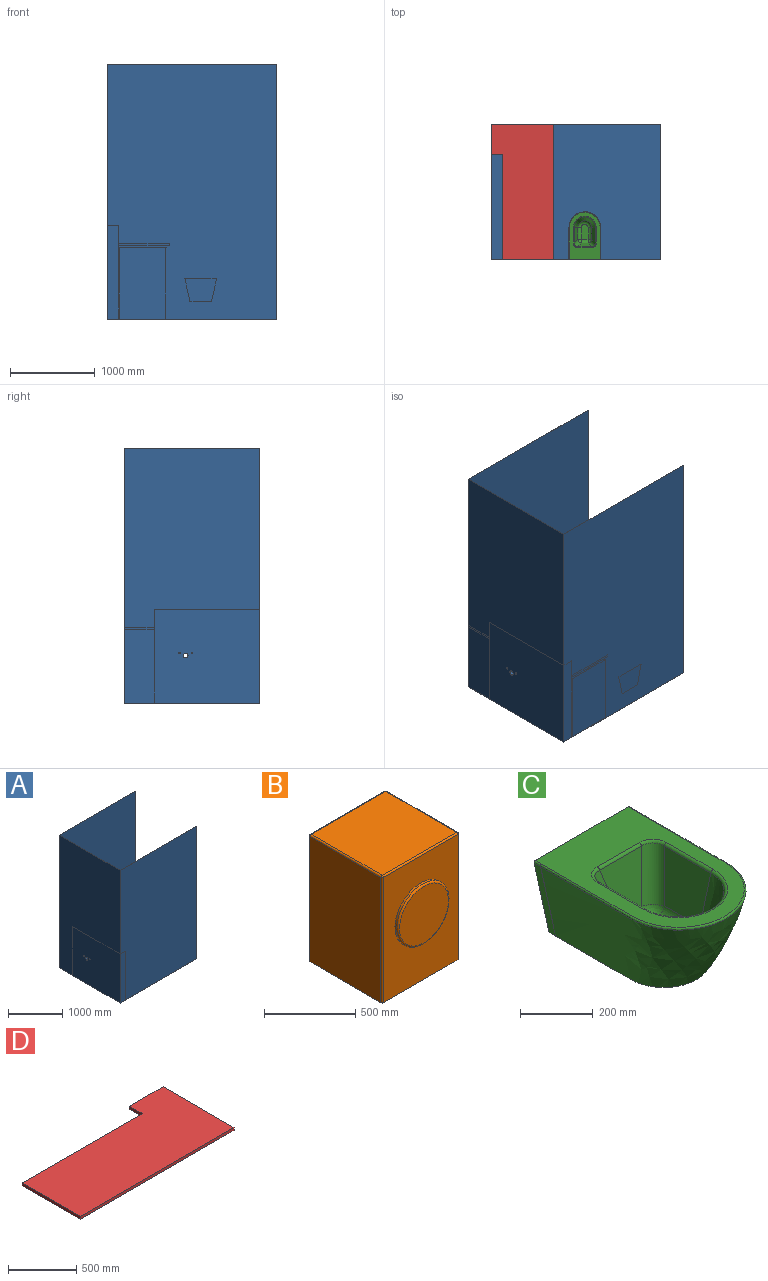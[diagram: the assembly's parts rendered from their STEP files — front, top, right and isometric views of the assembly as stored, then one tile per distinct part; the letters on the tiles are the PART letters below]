
ASSEMBLY  parts=4 mates=3
PART A: 30 faces, bbox 2000x1593x3000 mm
  f0: plane 27x12.73mm, normal (1,0,0), area 104.7mm2, adj f15,f18,f19
  f1: plane 645x85mm, normal (1,0,0), area 51115.5mm2, adj f10,f15,f17,f18,f19
  f2: plane 1999x1591mm, normal (0,0,1), area 3016465mm2, adj f3,f5,f10,f11,f12,f13
  f3: plane 2999x1591mm, normal (1,0,0), area 3398999mm2, adj f2,f4,f10,f11,f13,f14
  f4: plane 2000x1593mm, normal (0,0,1), area 5591mm2, adj f3,f5,f6,f7,f8,f10,f11
  f5: plane 3000x1593mm, normal (1,0,0), area 7591mm2, adj f2,f4,f6,f8,f9,f10,f11
  f6: plane 3000x2000mm, normal (0,1,0), area 6000000mm2, adj f4,f5,f7,f9
  f7: plane 3000x1593mm, normal (-1,0,0), area 4776115.2mm2, adj f4,f6,f8,f9,f22,f28,f29
  f8: plane 3000x2000mm, normal (0,-1,0), area 6000000mm2, adj f4,f5,f7,f9
  f9: plane 2000x1593mm, normal (0,0,-1), area 3186000mm2, adj f5,f6,f7,f8
  f10: plane 2999x1999mm, normal (0,-1,0), area 5733776mm2, adj f1,f2,f3,f4,f5,f15,f16,f17
  f11: plane 2999x1999mm, normal (0,1,0), area 5849141mm2, adj f2,f3,f4,f5,f12,f14
  f12: plane 1242x1105mm, normal (1,0,0), area 1369525.2mm2, adj f2,f11,f13,f14,f22,f28,f29
  f13: plane 1105x132mm, normal (0,1,0), area 145860mm2, adj f2,f3,f12,f14
  f14: plane 1242x132mm, normal (0,0,1), area 163944mm2, adj f3,f11,f12,f13
  f15: plane 405x85mm, normal (0,0,1), area 34425mm2, adj f0,f1,f10,f16,f18,f21
  f16: plane 645x85mm, normal (-1,0,0), area 54825mm2, adj f10,f15,f17,f18
  f17: plane 405x85mm, normal (0,0,-1), area 34425mm2, adj f1,f10,f16,f18
  f18: plane 645x405mm, normal (0,-1,0), area 256950mm2, adj f0,f1,f15,f16,f17,f23,f24,f25
  f19: cylinder r=35mm len=95mm, axis (-1,0,0), area 20891.6mm2, adj f0,f1,f20,f21
  f20: plane 70x70mm, normal (1,0,0), area 3848.5mm2, adj f19
  f21: plane 44.54x8mm, normal (-1,0,0), area 243.6mm2, adj f15,f19
  f22: cylinder r=27.5mm len=133mm, axis (1,0,0), area 22980.8mm2, adj f7,f12
  f23: plane 45x30mm, normal (0,0,1), area 1350mm2, adj f18,f24,f26,f27
  f24: plane 95x30mm, normal (-1,0,0), area 2850mm2, adj f18,f23,f25,f27
  f25: plane 45x30mm, normal (0,0,-1), area 1350mm2, adj f18,f24,f26,f27
  f26: plane 95x30mm, normal (1,0,0), area 2850mm2, adj f18,f23,f25,f27
  f27: plane 95x45mm, normal (0,-1,0), area 4275mm2, adj f23,f24,f25,f26
  f28: cylinder r=9mm len=133mm, axis (1,0,0), area 7521mm2, adj f7,f12
  f29: cylinder r=9mm len=133mm, axis (1,0,0), area 7521mm2, adj f7,f12
PART B: 21 faces, bbox 597x595x850 mm
  f0: plane 577x550mm, normal (0,0,1), area 317350mm2, adj f11,f14,f17,f20
  f1: plane 840x550mm, normal (-1,0,0), area 462000mm2, adj f2,f15,f16,f20
  f2: plane 597x570mm, normal (0,0,-1), area 340204.2mm2, adj f1,f3,f4,f5,f9,f10,f15,f16
  f3: plane 840x550mm, normal (1,0,0), area 462000mm2, adj f2,f9,f10,f11
  f4: plane 840x577mm, normal (0,-1,0), area 359016.3mm2, adj f2,f6,f9,f14,f15
  f5: plane 840x577mm, normal (0,1,0), area 484680mm2, adj f2,f10,f16,f17
  f6: cylinder r=200mm len=400mm, axis (0,1,0), area 18221.2mm2, adj f4,f8
  f7: plane 379x379mm, normal (0,-1,0), area 112815.4mm2, adj f8
  f8: torus R=189.5mm, axis (0,-1,0), area 20330.8mm2, adj f6,f7
  f9: cylinder r=10mm len=840mm, axis (0,0,-1), area 13194.7mm2, adj f2,f3,f4,f12
  f10: cylinder r=10mm len=840mm, axis (0,0,1), area 13194.7mm2, adj f2,f3,f5,f13
  f11: cylinder r=10mm len=550mm, axis (0,1,0), area 8639.4mm2, adj f0,f3,f12,f13
  f12: sphere r=10mm, area 157.1mm2, adj f9,f11,f14
  f13: sphere r=10mm, area 157.1mm2, adj f10,f11,f17
  f14: cylinder r=10mm len=577mm, axis (1,0,0), area 9063.5mm2, adj f0,f4,f12,f18
  f15: cylinder r=10mm len=840mm, axis (0,0,1), area 13194.7mm2, adj f1,f2,f4,f18
  f16: cylinder r=10mm len=840mm, axis (0,0,-1), area 13194.7mm2, adj f1,f2,f5,f19
  f17: cylinder r=10mm len=577mm, axis (-1,0,0), area 9063.5mm2, adj f0,f5,f13,f19
  f18: sphere r=10mm, area 157.1mm2, adj f14,f15,f20
  f19: sphere r=10mm, area 157.1mm2, adj f16,f17,f20
  f20: cylinder r=10mm len=550mm, axis (0,-1,0), area 8639.4mm2, adj f0,f1,f18,f19
PART C: 30 faces, bbox 409.3x644.8x304.3 mm
  f0: plane 558.49x362.53mm, normal (0,0,1), area 97226.2mm2, adj f3,f6,f7,f8,f9,f10,f24,f25
  f1: plane 453.07x260.57mm, normal (0,0,-1), area 107135mm2, adj f2,f4,f5,f7
  f2: bspline ~565x375mm, area 311654.4mm2, adj f1,f3,f6,f8
  f3: plane 304.29x93.05mm, normal (0,-1,0), area 190.7mm2, adj f0,f2,f4,f8,f10
  f4: plane 263.92x58.65mm, normal (0.98,0,-0.22), area 6758.8mm2, adj f1,f3,f7,f10
  f5: plane 263.92x58.65mm, normal (-0.98,0,-0.22), area 6758.8mm2, adj f1,f6,f7,f9
  f6: plane 304.29x93.05mm, normal (0,-1,0), area 190.7mm2, adj f0,f2,f5,f8,f9
  f7: plane 372.53x270mm, normal (0,1,0), area 85032.4mm2, adj f0,f1,f4,f5,f9,f10
  f8: bspline ~610.52x375mm, area 11613.7mm2, adj f0,f2,f3,f6
  f9: cylinder r=5mm len=25mm, axis (0,-1,0), area 223.7mm2, adj f0,f5,f6,f7
  f10: cylinder r=5mm len=25mm, axis (0,1,0), area 223.7mm2, adj f0,f3,f4,f7
  f11: plane 164.09x159.24mm, normal (0,-0.97,0.26), area 20017.6mm2, adj f16,f20,f23,f25
  f12: plane 182.05x159.24mm, normal (0.97,0,0.26), area 26494mm2, adj f13,f21,f23,f26
  f13: cone r=127.5mm half-angle=15deg, axis (0,0,1), area 53955mm2, adj f12,f14,f19,f28
  f14: plane 182.05x159.24mm, normal (-0.97,0,0.26), area 26494mm2, adj f13,f16,f17,f29
  f15: plane 178.76x78.76mm, normal (0,0,1), area 13413.8mm2, adj f17,f19,f20,f21
  f16: cylinder r=45mm len=163.53mm, axis (-0.25,-0.25,-0.94), area 11523mm2, adj f11,f14,f18,f27
  f17: cylinder r=45mm len=139.38mm, axis (0,-1,0), area 8210.2mm2, adj f14,f15,f18,f19
  f18: sphere r=45mm, area 1523.9mm2, adj f16,f17,f20
  f19: torus R=39.38mm, axis (0,0,1), area 12002.7mm2, adj f13,f15,f17,f21
  f20: cylinder r=45mm len=78.76mm, axis (1,0,0), area 4639.4mm2, adj f11,f15,f18,f22
  f21: cylinder r=45mm len=139.38mm, axis (0,-1,0), area 8210.2mm2, adj f12,f15,f19,f22
  f22: sphere r=45mm, area 3778.9mm2, adj f20,f21,f23
  f23: cylinder r=45mm len=163.53mm, axis (0.25,-0.25,-0.94), area 11523mm2, adj f11,f12,f22,f24
  f24: bspline ~53.13x53.13mm, area 934.1mm2, adj f0,f23,f25,f26
  f25: cylinder r=10mm len=164.09mm, axis (-1,0,0), area 2148mm2, adj f0,f11,f24,f27
  f26: cylinder r=10mm len=182.05mm, axis (0,1,0), area 2383mm2, adj f0,f12,f24,f28
  f27: bspline ~53.13x53.13mm, area 934.1mm2, adj f0,f16,f25,f29
  f28: torus R=135.17mm, axis (0,0,1), area 5325.9mm2, adj f0,f13,f26,f29
  f29: cylinder r=10mm len=182.05mm, axis (0,1,0), area 2383mm2, adj f0,f14,f27,f28
PART D: 8 faces, bbox 1591x732x25 mm
  f0: plane 349x25mm, normal (0,1,0), area 8725mm2, adj f1,f5,f6,f7
  f1: plane 132x25mm, normal (-1,0,0), area 3300mm2, adj f0,f2,f6,f7
  f2: plane 1242x25mm, normal (0,1,0), area 31050mm2, adj f1,f3,f6,f7
  f3: plane 600x25mm, normal (-1,0,0), area 15000mm2, adj f2,f4,f6,f7
  f4: plane 1591x25mm, normal (0,-1,0), area 39775mm2, adj f3,f5,f6,f7
  f5: plane 732x25mm, normal (1,0,0), area 18300mm2, adj f0,f4,f6,f7
  f6: plane 1591x732mm, normal (0,0,1), area 1000668mm2, adj f0,f1,f2,f3,f4,f5
  f7: plane 1591x732mm, normal (0,0,-1), area 1000668mm2, adj f0,f1,f2,f3,f4,f5
PLACE A t=(-2157.21,470.22,-631.04)mm fixed
PLACE B rot(axis=(0,0,1),90deg) t=(-2739.21,-821.28,-630.04)mm
PLACE C rot(axis=(0,0,-1),180deg) t=(-2054.21,-1121.78,-150.04)mm
PLACE D rot(axis=(0,0,1),90deg) t=(-3120.42,102.97,234.96)mm
MATE fastened D.f2 <-> A.f12  axis (-1,0,0) through (-3024.21,-1121.78,259.96)mm
MATE fastened B.f5 <-> A.f12  axis (-1,0,0) through (-3024.21,-1109.78,-630.04)mm
MATE fastened C.f7 <-> A.f11  axis (0,-1,0) through (-2054.21,-1121.78,-150.04)mm
